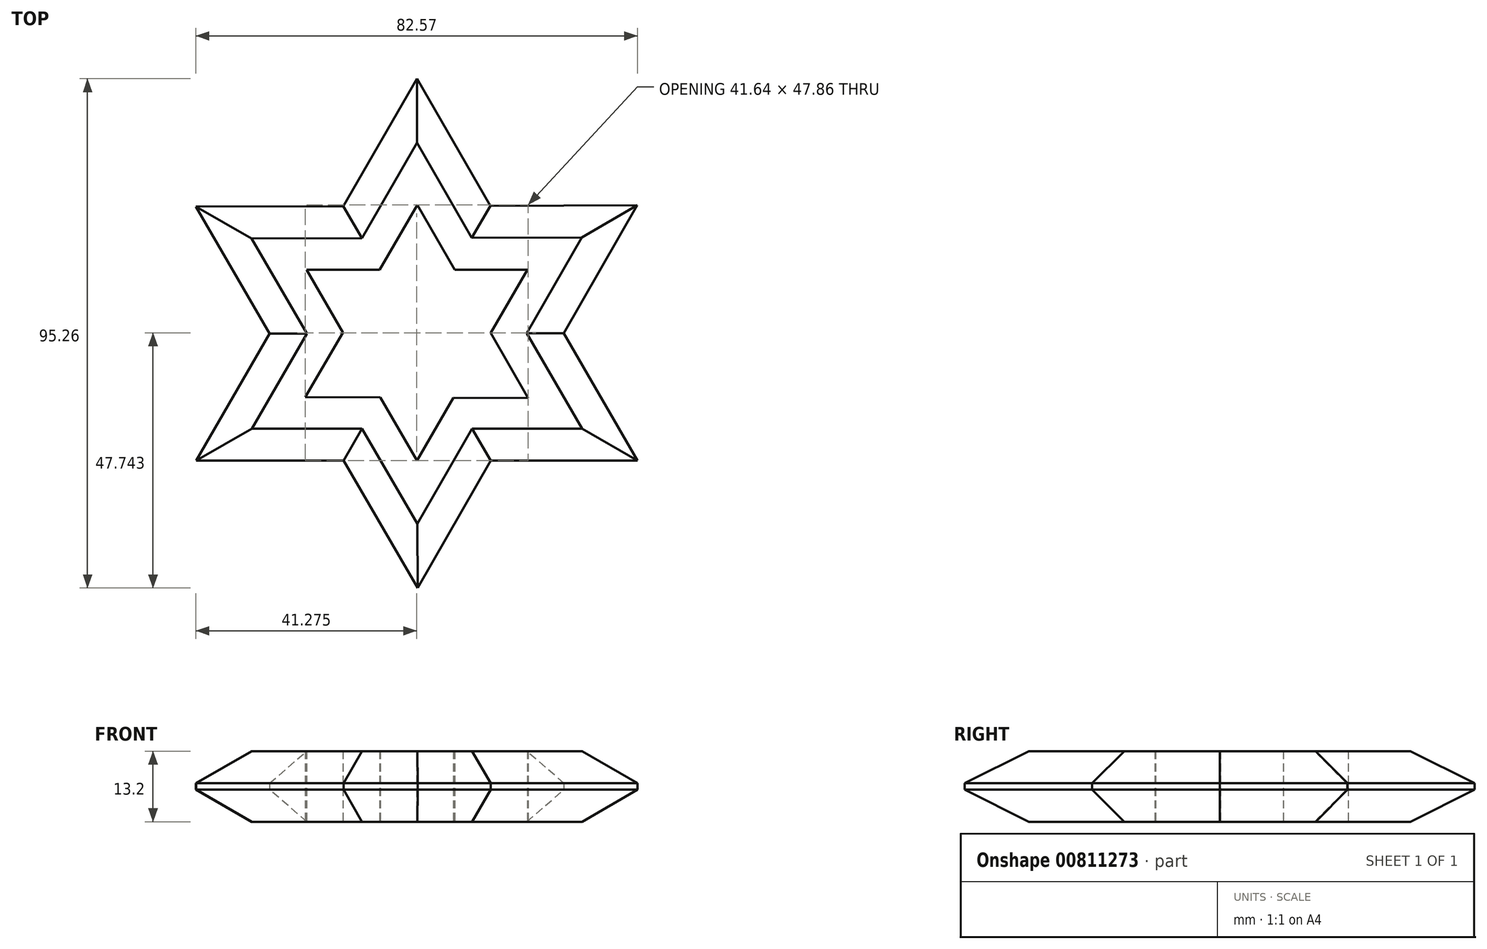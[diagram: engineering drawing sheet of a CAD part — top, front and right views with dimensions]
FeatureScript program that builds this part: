
annotation { "Feature Type Name" : "Feature", "Feature Type Description" : "" }
export const myFeature = defineFeature(function(context is Context, id is Id, definition is map)
    precondition{}
    {
        {
            var Q0;
            Q0=qCreatedBy(makeId("Top.planeOp"),FACE);
            var sketch = newSketch(context, id + "F0", { "sketchPlane" : qUnion([Q0])});
            skCircle(sketch, "E0", {"center": v(0, 0) * mm, "radius": 11.1 * mm});
            skLineSegment(sketch, "E1.0", {"start": v(-20.87, -11.94) * mm, "end": v(-13.83, 0.14) * mm});
            skLineSegment(sketch, "E1.1", {"start": v(0.09, 24.04) * mm, "end": v(7.04, 11.9) * mm});
            skLineSegment(sketch, "E1.2", {"start": v(20.78, -12.1) * mm, "end": v(6.8, -12.05) * mm});
            skLineSegment(sketch, "E2.0", {"start": v(0, 47.63) * mm, "end": v(13.73, 23.85) * mm});
            skLineSegment(sketch, "E2.1", {"start": v(41.25, -23.82) * mm, "end": v(13.8, -23.82) * mm});
            skLineSegment(sketch, "E2.2", {"start": v(-41.25, -23.82) * mm, "end": v(-27.52, -0.04) * mm});
            skLineSegment(sketch, "E3.0", {"start": v(-41.32, 23.7) * mm, "end": v(-13.77, 23.78) * mm});
            skLineSegment(sketch, "E3.1", {"start": v(41.18, 23.93) * mm, "end": v(27.48, 0.04) * mm});
            skLineSegment(sketch, "E3.2", {"start": v(0.13, -47.63) * mm, "end": v(-13.7, -23.82) * mm});
            skArc(sketch, "E4.cCircle", {"start": v(-20.73, -11.72) * mm, "mid": v(-20.66, -11.84) * mm, "end": v(-20.6, -11.97) * mm, "construction": true});
            skLineSegment(sketch, "E4.0", {"start": v(-20.63, 11.9) * mm, "end": v(-6.98, 11.9) * mm});
            skLineSegment(sketch, "E4.1", {"start": v(20.63, 11.9) * mm, "end": v(13.8, 0.09) * mm});
            skLineSegment(sketch, "E4.2", {"start": v(0, -23.82) * mm, "end": v(-6.82, -12) * mm});
            skArc(sketch, "E5.trimOffspring", {"start": v(0.22, 23.81) * mm, "mid": v(0.08, 23.82) * mm, "end": v(-0.07, 23.82) * mm, "construction": true});
            skArc(sketch, "E6.trimOffspring", {"start": v(20.51, -12.1) * mm, "mid": v(20.59, -11.97) * mm, "end": v(20.66, -11.85) * mm, "construction": true});
            skLineSegment(sketch, "E7.trimOffspring", {"start": v(-13.77, 23.78) * mm, "end": v(0, 47.63) * mm});
            skLineSegment(sketch, "E8.trimOffspring", {"start": v(-0.07, 23.82) * mm, "end": v(0.22, 23.82) * mm});
            skLineSegment(sketch, "E9.trimOffspring", {"start": v(13.73, 23.85) * mm, "end": v(41.18, 23.93) * mm});
            skLineSegment(sketch, "E10.trimOffspring", {"start": v(27.48, 0.04) * mm, "end": v(41.25, -23.82) * mm});
            skLineSegment(sketch, "E11.trimOffspring", {"start": v(20.66, -11.85) * mm, "end": v(20.52, -12.1) * mm});
            skLineSegment(sketch, "E12.trimOffspring", {"start": v(13.8, -23.82) * mm, "end": v(0.13, -47.63) * mm});
            skLineSegment(sketch, "E13.trimOffspring", {"start": v(-13.7, -23.82) * mm, "end": v(-41.25, -23.82) * mm});
            skLineSegment(sketch, "E14.trimOffspring", {"start": v(-20.6, -11.97) * mm, "end": v(-20.74, -11.72) * mm});
            skLineSegment(sketch, "E15.trimOffspring", {"start": v(-27.52, -0.04) * mm, "end": v(-41.32, 23.7) * mm});
            skLineSegment(sketch, "E16.trimOffspring", {"start": v(7.04, 11.9) * mm, "end": v(20.63, 11.9) * mm});
            skLineSegment(sketch, "E17.trimOffspring", {"start": v(-6.98, 11.9) * mm, "end": v(0.09, 24.04) * mm});
            skLineSegment(sketch, "E18.trimOffspring", {"start": v(-13.83, 0.14) * mm, "end": v(-20.63, 11.9) * mm});
            skLineSegment(sketch, "E19.trimOffspring", {"start": v(-6.82, -12) * mm, "end": v(-20.87, -11.94) * mm});
            skLineSegment(sketch, "E20.trimOffspring", {"start": v(6.8, -12.05) * mm, "end": v(0, -23.82) * mm});
            skLineSegment(sketch, "E21.trimOffspring", {"start": v(13.8, 0.09) * mm, "end": v(20.78, -12.1) * mm});
            skSolve(sketch);
        }
        {
            var Q0;
            Q0=makeQuery(id+"F0.imprint","IMPRINT",FACE,{"disambiguationData":[TD([[makeQuery(id+"F0.imprint","IMPRINT",EDGE,{"derivedFrom":sQuery(id+"F0.wireOp",EDGE,"E2.0")}),-1.0]])]});
            extrude(context, id + "F1", {"entities" : qUnion([Q0]), "depth" : 13.2 * mm, "offsetDistance" : 25 * mm});
        }
        {
            var Q0;
            Q0=makeQuery(id+"F1.opExtrude","CAP_EDGE",EDGE,{"disambiguationData":[OSD([sQuery(id+"F0.wireOp",EDGE,"E3.2")])],"isStart":true});
            var Q1;
            Q1=makeQuery(id+"F1.opExtrude","CAP_EDGE",EDGE,{"disambiguationData":[OSD([sQuery(id+"F0.wireOp",EDGE,"E13.trimOffspring")])],"isStart":true});
            var Q2;
            Q2=makeQuery(id+"F1.opExtrude","CAP_EDGE",EDGE,{"disambiguationData":[OSD([sQuery(id+"F0.wireOp",EDGE,"E12.trimOffspring")])],"isStart":true});
            var Q3;
            Q3=makeQuery(id+"F1.opExtrude","CAP_EDGE",EDGE,{"disambiguationData":[OSD([sQuery(id+"F0.wireOp",EDGE,"E2.1")])],"isStart":true});
            var Q4;
            Q4=makeQuery(id+"F1.opExtrude","CAP_EDGE",EDGE,{"disambiguationData":[OSD([sQuery(id+"F0.wireOp",EDGE,"E10.trimOffspring")])],"isStart":true});
            var Q5;
            Q5=makeQuery(id+"F1.opExtrude","CAP_EDGE",EDGE,{"disambiguationData":[OSD([sQuery(id+"F0.wireOp",EDGE,"E3.1")])],"isStart":true});
            var Q6;
            Q6=makeQuery(id+"F1.opExtrude","CAP_EDGE",EDGE,{"disambiguationData":[OSD([sQuery(id+"F0.wireOp",EDGE,"E9.trimOffspring")])],"isStart":true});
            var Q7;
            Q7=makeQuery(id+"F1.opExtrude","CAP_EDGE",EDGE,{"disambiguationData":[OSD([sQuery(id+"F0.wireOp",EDGE,"E2.0")])],"isStart":true});
            var Q8;
            Q8=makeQuery(id+"F1.opExtrude","CAP_EDGE",EDGE,{"disambiguationData":[OSD([sQuery(id+"F0.wireOp",EDGE,"E7.trimOffspring")])],"isStart":true});
            var Q9;
            Q9=makeQuery(id+"F1.opExtrude","CAP_EDGE",EDGE,{"disambiguationData":[OSD([sQuery(id+"F0.wireOp",EDGE,"E3.0")])],"isStart":true});
            var Q10;
            Q10=makeQuery(id+"F1.opExtrude","CAP_EDGE",EDGE,{"disambiguationData":[OSD([sQuery(id+"F0.wireOp",EDGE,"E15.trimOffspring")])],"isStart":true});
            var Q11;
            Q11=makeQuery(id+"F1.opExtrude","CAP_EDGE",EDGE,{"disambiguationData":[OSD([sQuery(id+"F0.wireOp",EDGE,"E2.2")])],"isStart":true});
            var Q12;
            Q12=makeQuery(id+"F1.opExtrude","CAP_EDGE",EDGE,{"disambiguationData":[OSD([sQuery(id+"F0.wireOp",EDGE,"E12.trimOffspring")])],"isStart":false});
            var Q13;
            Q13=makeQuery(id+"F1.opExtrude","CAP_EDGE",EDGE,{"disambiguationData":[OSD([sQuery(id+"F0.wireOp",EDGE,"E2.1")])],"isStart":false});
            var Q14;
            Q14=makeQuery(id+"F1.opExtrude","CAP_EDGE",EDGE,{"disambiguationData":[OSD([sQuery(id+"F0.wireOp",EDGE,"E10.trimOffspring")])],"isStart":false});
            var Q15;
            Q15=makeQuery(id+"F1.opExtrude","CAP_EDGE",EDGE,{"disambiguationData":[OSD([sQuery(id+"F0.wireOp",EDGE,"E3.1")])],"isStart":false});
            var Q16;
            Q16=makeQuery(id+"F1.opExtrude","CAP_EDGE",EDGE,{"disambiguationData":[OSD([sQuery(id+"F0.wireOp",EDGE,"E9.trimOffspring")])],"isStart":false});
            var Q17;
            Q17=makeQuery(id+"F1.opExtrude","CAP_EDGE",EDGE,{"disambiguationData":[OSD([sQuery(id+"F0.wireOp",EDGE,"E2.0")])],"isStart":false});
            var Q18;
            Q18=makeQuery(id+"F1.opExtrude","CAP_EDGE",EDGE,{"disambiguationData":[OSD([sQuery(id+"F0.wireOp",EDGE,"E7.trimOffspring")])],"isStart":false});
            var Q19;
            Q19=makeQuery(id+"F1.opExtrude","CAP_EDGE",EDGE,{"disambiguationData":[OSD([sQuery(id+"F0.wireOp",EDGE,"E3.0")])],"isStart":false});
            var Q20;
            Q20=makeQuery(id+"F1.opExtrude","CAP_EDGE",EDGE,{"disambiguationData":[OSD([sQuery(id+"F0.wireOp",EDGE,"E15.trimOffspring")])],"isStart":false});
            var Q21;
            Q21=makeQuery(id+"F1.opExtrude","CAP_EDGE",EDGE,{"disambiguationData":[OSD([sQuery(id+"F0.wireOp",EDGE,"E2.2")])],"isStart":false});
            var Q22;
            Q22=makeQuery(id+"F1.opExtrude","CAP_EDGE",EDGE,{"disambiguationData":[OSD([sQuery(id+"F0.wireOp",EDGE,"E13.trimOffspring")])],"isStart":false});
            var Q23;
            Q23=makeQuery(id+"F1.opExtrude","CAP_EDGE",EDGE,{"disambiguationData":[OSD([sQuery(id+"F0.wireOp",EDGE,"E3.2")])],"isStart":false});
            chamfer(context, id + "F2", {"entities" : qUnion([Q0, Q1, Q2, Q3, Q4, Q5, Q6, Q7, Q8, Q9, Q10, Q11, Q12, Q13, Q14, Q15, Q16, Q17, Q18, Q19, Q20, Q21, Q22, Q23]), "width" : 6 * mm, "tangentPropagation" : true});
        }
    });
